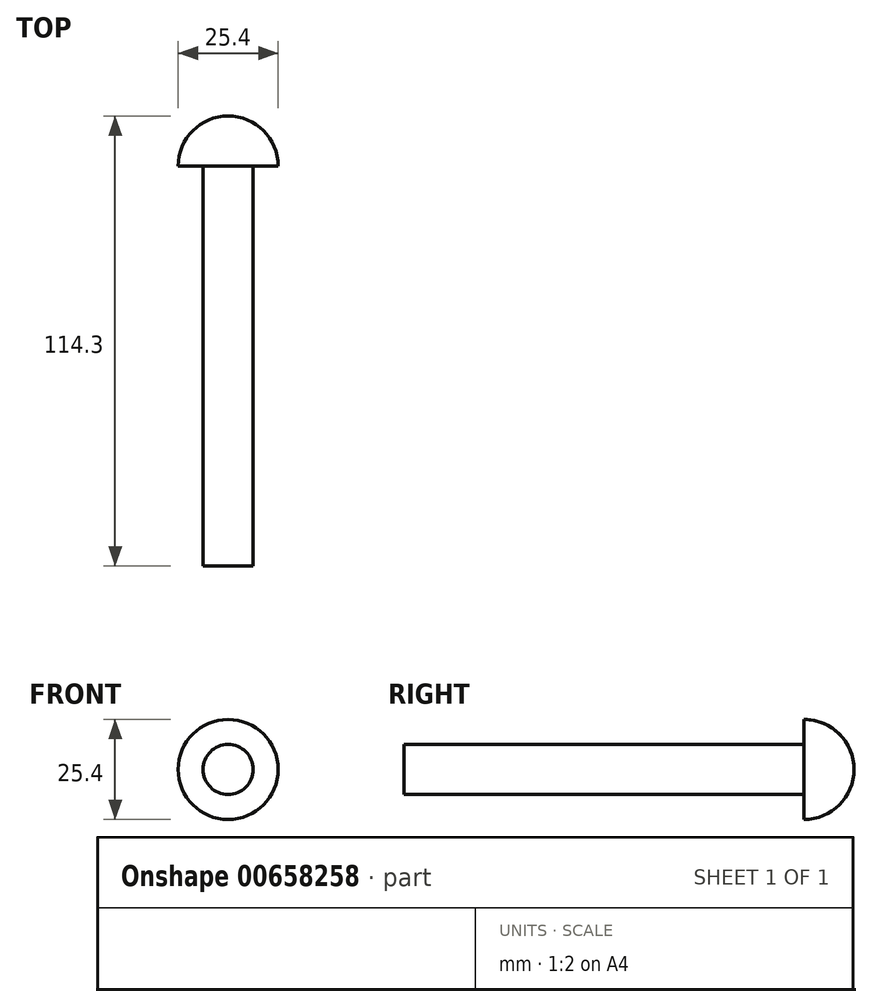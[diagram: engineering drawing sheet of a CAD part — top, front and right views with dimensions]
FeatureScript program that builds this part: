
annotation { "Feature Type Name" : "Feature", "Feature Type Description" : "" }
export const myFeature = defineFeature(function(context is Context, id is Id, definition is map)
    precondition{}
    {
        {
            var Q0;
            Q0=qCreatedBy(makeId("Front.planeOp"),FACE);
            var sketch = newSketch(context, id + "F0", { "sketchPlane" : qUnion([Q0])});
            skCircle(sketch, "E0", {"center": v(0, 0) * mm, "radius": 6.35 * mm});
            skSolve(sketch);
        }
        {
            var Q0;
            Q0 = qSketchRegion(id + "F0", true);
            extrude(context, id + "F1", {"entities" : qUnion([Q0]), "depth" : 101.6 * mm, "offsetDistance" : 25.4 * mm});
        }
        {
            var Q0;
            Q0=qCreatedBy(makeId("Right.planeOp"),FACE);
            var sketch = newSketch(context, id + "F2", { "sketchPlane" : qUnion([Q0])});
            skLineSegment(sketch, "E1", {"start": v(0, 0) * mm, "end": v(0, 12.7) * mm});
            skLineSegment(sketch, "E2", {"start": v(0, 0) * mm, "end": v(12.7, 0) * mm});
            skArc(sketch, "E3", {"start": v(0, 12.7) * mm, "mid": v(8.98, 8.98) * mm, "end": v(12.7, 0) * mm});
            skSolve(sketch);
        }
        {
            var Q0;
            Q0 = qSketchRegion(id + "F2", true);
            var Q1;
            Q1=sQuery(id+"F2.wireOp",EDGE,"E2");
            revolve(context, id + "F3", {"operationType" : NewBodyOperationType.ADD, "entities" : qUnion([Q0]), "axis" : qUnion([Q1]), "revolveType" : RevolveType.FULL});
        }
    });
